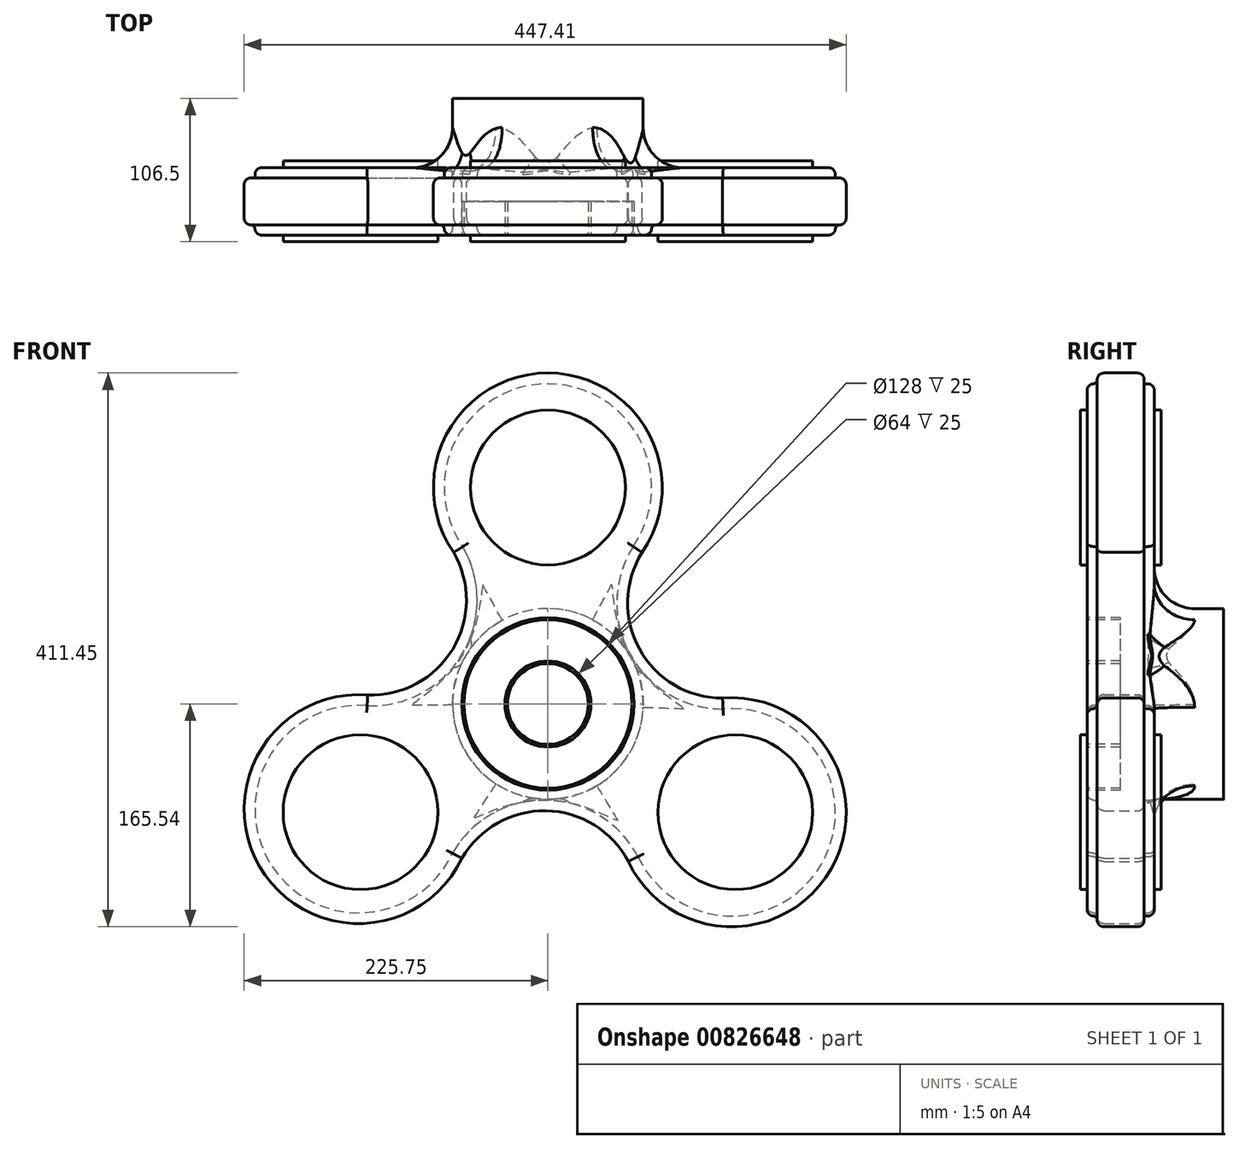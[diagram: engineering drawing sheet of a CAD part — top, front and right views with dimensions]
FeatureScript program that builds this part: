
annotation { "Feature Type Name" : "Feature", "Feature Type Description" : "" }
export const myFeature = defineFeature(function(context is Context, id is Id, definition is map)
    precondition{}
    {
        {
            var Q0;
            Q0=qCreatedBy(makeId("Front.planeOp"),FACE);
            var sketch = newSketch(context, id + "F0", { "sketchPlane" : qUnion([Q0])});
            skLineSegment(sketch, "E0", {"start": v(-407.93, 0) * mm, "end": v(423.02, 0) * mm, "construction": true});
            skLineSegment(sketch, "E1", {"start": v(-410.58, 247) * mm, "end": v(450.17, 247) * mm, "construction": true});
            skLineSegment(sketch, "E2", {"start": v(0, -266.9) * mm, "end": v(0, 261.2) * mm, "construction": true});
            skLineSegment(sketch, "E3", {"start": v(0, 0) * mm, "end": v(-359.58, -207.6) * mm, "construction": true});
            skLineSegment(sketch, "E4", {"start": v(0, 0) * mm, "end": v(372.56, -215.1) * mm, "construction": true});
            skCircle(sketch, "E5", {"center": v(0, 0) * mm, "radius": 50 * mm, "construction": true});
            skCircle(sketch, "E6", {"center": v(0, 160.84) * mm, "radius": 85 * mm, "construction": true});
            skCircle(sketch, "E7.1.0", {"center": v(-139.3, -80.42) * mm, "radius": 85 * mm, "construction": true});
            skCircle(sketch, "E7.2.0", {"center": v(139.3, -80.42) * mm, "radius": 85 * mm, "construction": true});
            skCircle(sketch, "E8", {"center": v(0, -149.9) * mm, "radius": 70 * mm, "construction": true});
            skCircle(sketch, "E9.1.0", {"center": v(129.82, 74.95) * mm, "radius": 70 * mm, "construction": true});
            skCircle(sketch, "E9.2.0", {"center": v(-129.82, 74.95) * mm, "radius": 70 * mm, "construction": true});
            skSolve(sketch);
        }
        {
            var Q0;
            Q0=qCreatedBy(makeId("Front.planeOp"),FACE);
            var sketch = newSketch(context, id + "F1", { "sketchPlane" : qUnion([Q0])});
            skPoint(sketch, "E10.0", {"position": v(-129.82, 74.95) * mm});
            skPoint(sketch, "E11.0", {"position": v(0, 160.84) * mm});
            skArc(sketch, "E12", {"start": v(-70.05, 112.58) * mm, "mid": v(-75.3, 200.4) * mm, "end": v(0, 245.9) * mm});
            skArc(sketch, "E13.MirrorCS", {"start": v(70.05, 112.58) * mm, "mid": v(75.3, 200.4) * mm, "end": v(0, 245.9) * mm});
            skArc(sketch, "E14.MirrorCS", {"start": v(70.05, 112.58) * mm, "mid": v(68, 40.82) * mm, "end": v(129.82, 4.32) * mm});
            skArc(sketch, "E15.1.0", {"start": v(-63.87, -114.64) * mm, "mid": v(-137.3, -163.1) * mm, "end": v(-214.36, -120.64) * mm});
            skArc(sketch, "E15.1.1", {"start": v(-133.92, 6.7) * mm, "mid": v(-212.6, -32.67) * mm, "end": v(-214.36, -120.64) * mm});
            skArc(sketch, "E15.1.2", {"start": v(-133.92, 6.7) * mm, "mid": v(-70.74, 40.79) * mm, "end": v(-70.05, 112.58) * mm});
            skArc(sketch, "E15.2.0", {"start": v(129.82, 4.32) * mm, "mid": v(208.5, -35.04) * mm, "end": v(210.26, -123) * mm});
            skArc(sketch, "E15.2.1", {"start": v(59.77, -117) * mm, "mid": v(133.2, -165.47) * mm, "end": v(210.26, -123) * mm});
            skArc(sketch, "E15.2.2", {"start": v(59.77, -117) * mm, "mid": v(-1.35, -79.34) * mm, "end": v(-63.87, -114.64) * mm});
            skPoint(sketch, "E15.center", {"position": v(-1.37, 0.75) * mm});
            skSolve(sketch);
        }
        {
            var Q0;
            Q0 = qSketchRegion(id + "F1", true);
            extrude(context, id + "F2", {"entities" : qUnion([Q0]), "endBound" : BoundingType.SYMMETRIC, "depth" : 35 * mm, "offsetDistance" : 25 * mm});
        }
        {
            var Q0;
            Q0=qCreatedBy(makeId("Front.planeOp"),FACE);
            var sketch = newSketch(context, id + "F3", { "sketchPlane" : qUnion([Q0])});
            skPoint(sketch, "E16.0", {"position": v(0, 160.84) * mm});
            skCircle(sketch, "E17", {"center": v(0, 160.84) * mm, "radius": 57.5 * mm});
            skCircle(sketch, "E18", {"center": v(0, 160.84) * mm, "radius": 50 * mm});
            skCircle(sketch, "E19.1.0", {"center": v(-139.3, -80.42) * mm, "radius": 57.5 * mm});
            skCircle(sketch, "E19.1.1", {"center": v(-139.3, -80.42) * mm, "radius": 50 * mm});
            skCircle(sketch, "E19.2.0", {"center": v(139.3, -80.42) * mm, "radius": 57.5 * mm});
            skCircle(sketch, "E19.2.1", {"center": v(139.3, -80.42) * mm, "radius": 50 * mm});
            skPoint(sketch, "E19.center", {"position": v(0, 0) * mm});
            skSolve(sketch);
        }
        {
            var Q0;
            Q0 = qSketchRegion(id + "F3", true);
            extrude(context, id + "F4", {"entities" : qUnion([Q0]), "endBound" : BoundingType.SYMMETRIC, "depth" : 60 * mm, "offsetDistance" : 25 * mm});
        }
        {
            var Q0;
            Q0=qCreatedBy(makeId("Front.planeOp"),FACE);
            var sketch = newSketch(context, id + "F5", { "sketchPlane" : qUnion([Q0])});
            skPoint(sketch, "E20.0", {"position": v(0, 160.84) * mm});
            skCircle(sketch, "E21", {"center": v(0, 160.84) * mm, "radius": 32.5 * mm});
            skCircle(sketch, "E22", {"center": v(0, 160.84) * mm, "radius": 17.5 * mm});
            skCircle(sketch, "E23.1.0", {"center": v(-139.3, -80.42) * mm, "radius": 32.5 * mm});
            skCircle(sketch, "E23.1.1", {"center": v(-139.3, -80.42) * mm, "radius": 17.5 * mm});
            skCircle(sketch, "E23.2.0", {"center": v(139.3, -80.42) * mm, "radius": 32.5 * mm});
            skCircle(sketch, "E23.2.1", {"center": v(139.3, -80.42) * mm, "radius": 17.5 * mm});
            skPoint(sketch, "E23.center", {"position": v(0, 0) * mm});
            skSolve(sketch);
        }
        {
            var Q0;
            Q0 = qSketchRegion(id + "F5", true);
            extrude(context, id + "F6", {"entities" : qUnion([Q0]), "endBound" : BoundingType.SYMMETRIC, "depth" : 60 * mm, "offsetDistance" : 25 * mm});
        }
        {
            var Q0;
            Q0=qCreatedBy(makeId("Front.planeOp"),FACE);
            var sketch = newSketch(context, id + "F7", { "sketchPlane" : qUnion([Q0])});
            skCircle(sketch, "E24.0", {"center": v(0, 160.84) * mm, "radius": 50 * mm});
            skCircle(sketch, "E25.0", {"center": v(0, 160.84) * mm, "radius": 32.5 * mm});
            skCircle(sketch, "E26.0", {"center": v(-139.3, -80.42) * mm, "radius": 50 * mm});
            skCircle(sketch, "E27.0", {"center": v(-139.3, -80.42) * mm, "radius": 32.5 * mm});
            skCircle(sketch, "E28.0", {"center": v(139.3, -80.42) * mm, "radius": 32.5 * mm});
            skCircle(sketch, "E29.0", {"center": v(139.3, -80.42) * mm, "radius": 50 * mm});
            skCircle(sketch, "E30.0", {"center": v(0, 160.84) * mm, "radius": 17.5 * mm});
            skCircle(sketch, "E31.0", {"center": v(-139.3, -80.42) * mm, "radius": 17.5 * mm});
            skCircle(sketch, "E32.0", {"center": v(139.3, -80.42) * mm, "radius": 17.5 * mm});
            skSolve(sketch);
        }
        {
            var Q0;
            Q0 = qSketchRegion(id + "F7", true);
            extrude(context, id + "F8", {"entities" : qUnion([Q0]), "operationType" : NewBodyOperationType.ADD, "endBound" : BoundingType.SYMMETRIC, "depth" : 60 * mm, "offsetDistance" : 25 * mm});
        }
        {
            var Q0;
            Q0=qCreatedBy(makeId("Front.planeOp"),FACE);
            var sketch = newSketch(context, id + "F9", { "sketchPlane" : qUnion([Q0])});
            skCircle(sketch, "E33.0", {"center": v(0, 160.84) * mm, "radius": 17.5 * mm});
            skCircle(sketch, "E33.1", {"center": v(-139.3, -80.42) * mm, "radius": 17.5 * mm});
            skCircle(sketch, "E33.2", {"center": v(139.3, -80.42) * mm, "radius": 17.5 * mm});
            skSolve(sketch);
        }
        {
            var Q0;
            Q0 = qSketchRegion(id + "F9", true);
            extrude(context, id + "F10", {"entities" : qUnion([Q0]), "operationType" : NewBodyOperationType.ADD, "endBound" : BoundingType.SYMMETRIC, "depth" : 60 * mm, "offsetDistance" : 25 * mm});
        }
        {
            var Q0;
            {var subQ0=sQuery(id+"F1.wireOp",EDGE,"E15.1.1");var subQ1=sQuery(id+"F1.wireOp",EDGE,"E15.1.0");var subQ2=sQuery(id+"F1.wireOp",EDGE,"E14.MirrorCS");var subQ3=sQuery(id+"F1.wireOp",EDGE,"E15.1.2");var subQ4=sQuery(id+"F1.wireOp",EDGE,"E13.MirrorCS");var subQ5=sQuery(id+"F1.wireOp",EDGE,"E12");var subQ6=sQuery(id+"F1.wireOp",EDGE,"E15.2.1");var subQ7=sQuery(id+"F1.wireOp",EDGE,"E15.2.0");var subQ8=sQuery(id+"F1.wireOp",EDGE,"E15.2.2");Q0=makeQuery(id+"F8.boolean.opBoolean","SPLIT",FACE,{"disambiguationData":[TD([makeQuery(id+"F2.opExtrude","SWEPT_FACE",FACE,{"disambiguationData":[OSD([subQ2])]})])],"derivedFrom":makeQuery(id+"F2.opExtrude","CAP_FACE",FACE,{"disambiguationData":[OSD([subQ5,subQ4,subQ2,subQ1,subQ0,subQ3,subQ7,subQ6,subQ8])],"isStart":true})});}
            var sketch = newSketch(context, id + "F11", { "sketchPlane" : qUnion([Q0])});
            skCircle(sketch, "E34", {"center": v(0, 0) * mm, "radius": 70.83 * mm});
            skSolve(sketch);
        }
        {
            var Q0;
            Q0 = qSketchRegion(id + "F11", true);
            extrude(context, id + "F12", {"entities" : qUnion([Q0]), "operationType" : NewBodyOperationType.ADD, "depth" : 59 * mm, "offsetDistance" : 25 * mm});
        }
        {
            var Q0;
            Q0=qCreatedBy(makeId("Front.planeOp"),FACE);
            var sketch = newSketch(context, id + "F13", { "sketchPlane" : qUnion([Q0])});
            skArc(sketch, "E35.0", {"start": v(63.37, 116.99) * mm, "mid": v(61.03, 36.88) * mm, "end": v(130.16, -3.67) * mm});
            skArc(sketch, "E35.1", {"start": v(-134.4, -1.3) * mm, "mid": v(-63.85, 36.73) * mm, "end": v(-63.3, 116.87) * mm});
            skArc(sketch, "E35.2", {"start": v(-134.4, -1.3) * mm, "mid": v(-207.4, -116.7) * mm, "end": v(-70.96, -110.93) * mm});
            skArc(sketch, "E35.3", {"start": v(63.37, 116.99) * mm, "mid": v(-0.07, 237.9) * mm, "end": v(-63.3, 116.87) * mm});
            skArc(sketch, "E35.4", {"start": v(66.93, -113.43) * mm, "mid": v(-1.28, -71.34) * mm, "end": v(-70.96, -110.93) * mm});
            skArc(sketch, "E35.5", {"start": v(66.93, -113.43) * mm, "mid": v(203.37, -118.94) * mm, "end": v(130.16, -3.67) * mm});
            skCircle(sketch, "E36.0", {"center": v(0, 160.84) * mm, "radius": 57.5 * mm});
            skCircle(sketch, "E37.0", {"center": v(-139.3, -80.42) * mm, "radius": 57.5 * mm});
            skCircle(sketch, "E38.0", {"center": v(139.3, -80.42) * mm, "radius": 57.5 * mm});
            skSolve(sketch);
        }
        {
            var Q0;
            Q0 = qSketchRegion(id + "F13", true);
            extrude(context, id + "F14", {"entities" : qUnion([Q0]), "operationType" : NewBodyOperationType.ADD, "endBound" : BoundingType.SYMMETRIC, "depth" : 50 * mm, "offsetDistance" : 25 * mm});
        }
        {
            var Q0;
            Q0=makeQuery(id+"F14.opExtrude","CAP_FACE",FACE,{"disambiguationData":[OSD([sQuery(id+"F13.wireOp",EDGE,"E35.0"),sQuery(id+"F13.wireOp",EDGE,"E35.1"),sQuery(id+"F13.wireOp",EDGE,"E35.2"),sQuery(id+"F13.wireOp",EDGE,"E35.3"),sQuery(id+"F13.wireOp",EDGE,"E35.4"),sQuery(id+"F13.wireOp",EDGE,"E35.5"),sQuery(id+"F13.wireOp",EDGE,"E36.0"),sQuery(id+"F13.wireOp",EDGE,"E37.0"),sQuery(id+"F13.wireOp",EDGE,"E38.0")])],"isStart":false});
            var sketch = newSketch(context, id + "F15", { "sketchPlane" : qUnion([Q0])});
            skCircle(sketch, "E39", {"center": v(0, 0) * mm, "radius": 64 * mm});
            skSolve(sketch);
        }
        {
            var Q0;
            Q0 = qSketchRegion(id + "F15", true);
            extrude(context, id + "F16", {"entities" : qUnion([Q0]), "operationType" : NewBodyOperationType.REMOVE, "oppositeDirection" : true, "depth" : 25 * mm, "offsetDistance" : 25 * mm});
        }
        {
            var Q0;
            Q0=makeQuery(id+"F14.opExtrude","CAP_FACE",FACE,{"disambiguationData":[OSD([sQuery(id+"F13.wireOp",EDGE,"E35.0"),sQuery(id+"F13.wireOp",EDGE,"E35.1"),sQuery(id+"F13.wireOp",EDGE,"E35.2"),sQuery(id+"F13.wireOp",EDGE,"E35.3"),sQuery(id+"F13.wireOp",EDGE,"E35.4"),sQuery(id+"F13.wireOp",EDGE,"E35.5"),sQuery(id+"F13.wireOp",EDGE,"E36.0"),sQuery(id+"F13.wireOp",EDGE,"E37.0"),sQuery(id+"F13.wireOp",EDGE,"E38.0")])],"isStart":false});
            var sketch = newSketch(context, id + "F17", { "sketchPlane" : qUnion([Q0])});
            skCircle(sketch, "E40", {"center": v(0, 0) * mm, "radius": 62.5 * mm});
            skSolve(sketch);
        }
        {
            var Q0;
            Q0 = qSketchRegion(id + "F17", true);
            extrude(context, id + "F18", {"entities" : qUnion([Q0]), "operationType" : NewBodyOperationType.ADD, "oppositeDirection" : true, "depth" : 37 * mm, "offsetDistance" : 25 * mm});
        }
        {
            var Q0;
            Q0=makeQuery(id+"F2.opExtrude","CAP_EDGE",EDGE,{"disambiguationData":[OSD([sQuery(id+"F1.wireOp",EDGE,"E12"),sQuery(id+"F1.wireOp",EDGE,"E13.MirrorCS")])],"isStart":false});
            var Q1;
            Q1=makeQuery(id+"F2.opExtrude","CAP_EDGE",EDGE,{"disambiguationData":[OSD([sQuery(id+"F1.wireOp",EDGE,"E15.1.0"),sQuery(id+"F1.wireOp",EDGE,"E15.1.1")])],"isStart":false});
            var Q2;
            Q2=makeQuery(id+"F2.opExtrude","CAP_EDGE",EDGE,{"disambiguationData":[OSD([sQuery(id+"F1.wireOp",EDGE,"E15.2.0"),sQuery(id+"F1.wireOp",EDGE,"E15.2.1")])],"isStart":false});
            var Q3;
            Q3=makeQuery(id+"F2.opExtrude","CAP_EDGE",EDGE,{"disambiguationData":[OSD([sQuery(id+"F1.wireOp",EDGE,"E15.2.0"),sQuery(id+"F1.wireOp",EDGE,"E15.2.1")])],"isStart":true});
            var Q4;
            Q4=makeQuery(id+"F2.opExtrude","CAP_EDGE",EDGE,{"disambiguationData":[OSD([sQuery(id+"F1.wireOp",EDGE,"E15.1.0"),sQuery(id+"F1.wireOp",EDGE,"E15.1.1")])],"isStart":true});
            var Q5;
            Q5=makeQuery(id+"FlsZefj5eaNXOrE_7.opFillet","BLEND_EDGE",EDGE,{"blendedFrom":[makeQuery(id+"F12.opExtrude","CAP_EDGE",EDGE,{"disambiguationData":[OSD([sQuery(id+"F11.wireOp",EDGE,"E34")])],"isStart":true}),makeQuery(id+"F2.opExtrude","SWEPT_FACE",FACE,{"disambiguationData":[OSD([sQuery(id+"F1.wireOp",EDGE,"E15.2.2")])]})],"blendedInto":[makeQuery(id+"F2.opExtrude","SWEPT_FACE",FACE,{"disambiguationData":[OSD([sQuery(id+"F1.wireOp",EDGE,"E15.2.2")])]})]});
            var Q6;
            Q6=makeQuery(id+"FlsZefj5eaNXOrE_7.opFillet","BLEND_EDGE",EDGE,{"blendedFrom":[makeQuery(id+"F12.opExtrude","CAP_EDGE",EDGE,{"disambiguationData":[OSD([sQuery(id+"F11.wireOp",EDGE,"E34")])],"isStart":true}),makeQuery(id+"F2.opExtrude","SWEPT_FACE",FACE,{"disambiguationData":[OSD([sQuery(id+"F1.wireOp",EDGE,"E14.MirrorCS")])]})],"blendedInto":[makeQuery(id+"F2.opExtrude","SWEPT_FACE",FACE,{"disambiguationData":[OSD([sQuery(id+"F1.wireOp",EDGE,"E14.MirrorCS")])]})]});
            var Q7;
            Q7=makeQuery(id+"F2.opExtrude","CAP_EDGE",EDGE,{"disambiguationData":[OSD([sQuery(id+"F1.wireOp",EDGE,"E12"),sQuery(id+"F1.wireOp",EDGE,"E13.MirrorCS")])],"isStart":true});
            var Q8;
            Q8=makeQuery(id+"FlsZefj5eaNXOrE_7.opFillet","BLEND_EDGE",EDGE,{"blendedFrom":[makeQuery(id+"F12.opExtrude","CAP_EDGE",EDGE,{"disambiguationData":[OSD([sQuery(id+"F11.wireOp",EDGE,"E34")])],"isStart":true}),makeQuery(id+"F2.opExtrude","SWEPT_FACE",FACE,{"disambiguationData":[OSD([sQuery(id+"F1.wireOp",EDGE,"E15.1.2")])]})],"blendedInto":[makeQuery(id+"F2.opExtrude","SWEPT_FACE",FACE,{"disambiguationData":[OSD([sQuery(id+"F1.wireOp",EDGE,"E15.1.2")])]})]});
            fillet(context, id + "F19", {"entities" : qUnion([Q0, Q1, Q2, Q3, Q4, Q5, Q6, Q7, Q8]), "radius" : 5 * mm, "tangentPropagation" : true, "allowEdgeOverflow" : false});
        }
        {
            var Q0;
            {var subQ0=sQuery(id+"F1.wireOp",EDGE,"E15.1.1");var subQ1=sQuery(id+"F1.wireOp",EDGE,"E15.1.0");var subQ2=sQuery(id+"F1.wireOp",EDGE,"E14.MirrorCS");var subQ3=sQuery(id+"F1.wireOp",EDGE,"E15.1.2");var subQ4=sQuery(id+"F1.wireOp",EDGE,"E13.MirrorCS");var subQ5=sQuery(id+"F1.wireOp",EDGE,"E12");var subQ6=sQuery(id+"F1.wireOp",EDGE,"E15.2.1");var subQ7=sQuery(id+"F1.wireOp",EDGE,"E15.2.0");var subQ8=sQuery(id+"F1.wireOp",EDGE,"E15.2.2");Q0=makeQuery(id+"F14.boolean.opBoolean","INTERSECT",EDGE,{"derivedFrom":[makeQuery(id+"F8.boolean.opBoolean","SPLIT",FACE,{"disambiguationData":[TD([makeQuery(id+"F2.opExtrude","SWEPT_FACE",FACE,{"disambiguationData":[OSD([subQ2])]})])],"derivedFrom":makeQuery(id+"F2.opExtrude","CAP_FACE",FACE,{"disambiguationData":[OSD([subQ5,subQ4,subQ2,subQ1,subQ0,subQ3,subQ7,subQ6,subQ8])],"isStart":false})}),makeQuery(id+"F14.opExtrude","SWEPT_FACE",FACE,{"disambiguationData":[OSD([sQuery(id+"F13.wireOp",EDGE,"E35.3")])]})]});}
            var Q1;
            {var subQ0=sQuery(id+"F1.wireOp",EDGE,"E15.1.1");var subQ1=sQuery(id+"F1.wireOp",EDGE,"E15.1.0");var subQ2=sQuery(id+"F1.wireOp",EDGE,"E14.MirrorCS");var subQ3=sQuery(id+"F1.wireOp",EDGE,"E15.1.2");var subQ4=sQuery(id+"F1.wireOp",EDGE,"E13.MirrorCS");var subQ5=sQuery(id+"F1.wireOp",EDGE,"E12");var subQ6=sQuery(id+"F1.wireOp",EDGE,"E15.2.1");var subQ7=sQuery(id+"F1.wireOp",EDGE,"E15.2.0");var subQ8=sQuery(id+"F1.wireOp",EDGE,"E15.2.2");Q1=makeQuery(id+"F14.boolean.opBoolean","INTERSECT",EDGE,{"derivedFrom":[makeQuery(id+"F8.boolean.opBoolean","SPLIT",FACE,{"disambiguationData":[TD([makeQuery(id+"F2.opExtrude","SWEPT_FACE",FACE,{"disambiguationData":[OSD([subQ2])]})])],"derivedFrom":makeQuery(id+"F2.opExtrude","CAP_FACE",FACE,{"disambiguationData":[OSD([subQ5,subQ4,subQ2,subQ1,subQ0,subQ3,subQ7,subQ6,subQ8])],"isStart":false})}),makeQuery(id+"F14.opExtrude","SWEPT_FACE",FACE,{"disambiguationData":[OSD([sQuery(id+"F13.wireOp",EDGE,"E35.1")])]})]});}
            var Q2;
            {var subQ0=sQuery(id+"F1.wireOp",EDGE,"E15.1.1");var subQ1=sQuery(id+"F1.wireOp",EDGE,"E15.1.0");var subQ2=sQuery(id+"F1.wireOp",EDGE,"E14.MirrorCS");var subQ3=sQuery(id+"F1.wireOp",EDGE,"E15.1.2");var subQ4=sQuery(id+"F1.wireOp",EDGE,"E13.MirrorCS");var subQ5=sQuery(id+"F1.wireOp",EDGE,"E12");var subQ6=sQuery(id+"F1.wireOp",EDGE,"E15.2.1");var subQ7=sQuery(id+"F1.wireOp",EDGE,"E15.2.0");var subQ8=sQuery(id+"F1.wireOp",EDGE,"E15.2.2");Q2=makeQuery(id+"F14.boolean.opBoolean","INTERSECT",EDGE,{"derivedFrom":[makeQuery(id+"F8.boolean.opBoolean","SPLIT",FACE,{"disambiguationData":[TD([makeQuery(id+"F2.opExtrude","SWEPT_FACE",FACE,{"disambiguationData":[OSD([subQ2])]})])],"derivedFrom":makeQuery(id+"F2.opExtrude","CAP_FACE",FACE,{"disambiguationData":[OSD([subQ5,subQ4,subQ2,subQ1,subQ0,subQ3,subQ7,subQ6,subQ8])],"isStart":false})}),makeQuery(id+"F14.opExtrude","SWEPT_FACE",FACE,{"disambiguationData":[OSD([sQuery(id+"F13.wireOp",EDGE,"E35.2")])]})]});}
            var Q3;
            {var subQ0=sQuery(id+"F1.wireOp",EDGE,"E15.1.1");var subQ1=sQuery(id+"F1.wireOp",EDGE,"E15.1.0");var subQ2=sQuery(id+"F1.wireOp",EDGE,"E14.MirrorCS");var subQ3=sQuery(id+"F1.wireOp",EDGE,"E15.1.2");var subQ4=sQuery(id+"F1.wireOp",EDGE,"E13.MirrorCS");var subQ5=sQuery(id+"F1.wireOp",EDGE,"E12");var subQ6=sQuery(id+"F1.wireOp",EDGE,"E15.2.1");var subQ7=sQuery(id+"F1.wireOp",EDGE,"E15.2.0");var subQ8=sQuery(id+"F1.wireOp",EDGE,"E15.2.2");Q3=makeQuery(id+"F14.boolean.opBoolean","INTERSECT",EDGE,{"derivedFrom":[makeQuery(id+"F8.boolean.opBoolean","SPLIT",FACE,{"disambiguationData":[TD([makeQuery(id+"F2.opExtrude","SWEPT_FACE",FACE,{"disambiguationData":[OSD([subQ2])]})])],"derivedFrom":makeQuery(id+"F2.opExtrude","CAP_FACE",FACE,{"disambiguationData":[OSD([subQ5,subQ4,subQ2,subQ1,subQ0,subQ3,subQ7,subQ6,subQ8])],"isStart":false})}),makeQuery(id+"F14.opExtrude","SWEPT_FACE",FACE,{"disambiguationData":[OSD([sQuery(id+"F13.wireOp",EDGE,"E35.4")])]})]});}
            var Q4;
            {var subQ0=sQuery(id+"F1.wireOp",EDGE,"E15.1.1");var subQ1=sQuery(id+"F1.wireOp",EDGE,"E15.1.0");var subQ2=sQuery(id+"F1.wireOp",EDGE,"E14.MirrorCS");var subQ3=sQuery(id+"F1.wireOp",EDGE,"E15.1.2");var subQ4=sQuery(id+"F1.wireOp",EDGE,"E13.MirrorCS");var subQ5=sQuery(id+"F1.wireOp",EDGE,"E12");var subQ6=sQuery(id+"F1.wireOp",EDGE,"E15.2.1");var subQ7=sQuery(id+"F1.wireOp",EDGE,"E15.2.0");var subQ8=sQuery(id+"F1.wireOp",EDGE,"E15.2.2");Q4=makeQuery(id+"F14.boolean.opBoolean","INTERSECT",EDGE,{"derivedFrom":[makeQuery(id+"F8.boolean.opBoolean","SPLIT",FACE,{"disambiguationData":[TD([makeQuery(id+"F2.opExtrude","SWEPT_FACE",FACE,{"disambiguationData":[OSD([subQ2])]})])],"derivedFrom":makeQuery(id+"F2.opExtrude","CAP_FACE",FACE,{"disambiguationData":[OSD([subQ5,subQ4,subQ2,subQ1,subQ0,subQ3,subQ7,subQ6,subQ8])],"isStart":false})}),makeQuery(id+"F14.opExtrude","SWEPT_FACE",FACE,{"disambiguationData":[OSD([sQuery(id+"F13.wireOp",EDGE,"E35.5")])]})]});}
            var Q5;
            {var subQ0=sQuery(id+"F1.wireOp",EDGE,"E15.1.1");var subQ1=sQuery(id+"F1.wireOp",EDGE,"E15.1.0");var subQ2=sQuery(id+"F1.wireOp",EDGE,"E14.MirrorCS");var subQ3=sQuery(id+"F1.wireOp",EDGE,"E15.1.2");var subQ4=sQuery(id+"F1.wireOp",EDGE,"E13.MirrorCS");var subQ5=sQuery(id+"F1.wireOp",EDGE,"E12");var subQ6=sQuery(id+"F1.wireOp",EDGE,"E15.2.1");var subQ7=sQuery(id+"F1.wireOp",EDGE,"E15.2.0");var subQ8=sQuery(id+"F1.wireOp",EDGE,"E15.2.2");Q5=makeQuery(id+"F14.boolean.opBoolean","INTERSECT",EDGE,{"derivedFrom":[makeQuery(id+"F8.boolean.opBoolean","SPLIT",FACE,{"disambiguationData":[TD([makeQuery(id+"F2.opExtrude","SWEPT_FACE",FACE,{"disambiguationData":[OSD([subQ2])]})])],"derivedFrom":makeQuery(id+"F2.opExtrude","CAP_FACE",FACE,{"disambiguationData":[OSD([subQ5,subQ4,subQ2,subQ1,subQ0,subQ3,subQ7,subQ6,subQ8])],"isStart":false})}),makeQuery(id+"F14.opExtrude","SWEPT_FACE",FACE,{"disambiguationData":[OSD([sQuery(id+"F13.wireOp",EDGE,"E35.0")])]})]});}
            fillet(context, id + "F20", {"entities" : qUnion([Q0, Q1, Q2, Q3, Q4, Q5]), "radius" : 3 * mm, "tangentPropagation" : true, "allowEdgeOverflow" : false});
        }
        {
            var Q0;
            Q0=makeQuery(id+"F14.opExtrude","CAP_EDGE",EDGE,{"disambiguationData":[OSD([sQuery(id+"F13.wireOp",EDGE,"E35.1")])],"isStart":false});
            var Q1;
            Q1=makeQuery(id+"F14.opExtrude","CAP_EDGE",EDGE,{"disambiguationData":[OSD([sQuery(id+"F13.wireOp",EDGE,"E35.3")])],"isStart":false});
            var Q2;
            Q2=makeQuery(id+"F14.opExtrude","CAP_EDGE",EDGE,{"disambiguationData":[OSD([sQuery(id+"F13.wireOp",EDGE,"E35.5")])],"isStart":false});
            var Q3;
            Q3=makeQuery(id+"F14.opExtrude","CAP_EDGE",EDGE,{"disambiguationData":[OSD([sQuery(id+"F13.wireOp",EDGE,"E35.2")])],"isStart":false});
            fillet(context, id + "F21", {"entities" : qUnion([Q0, Q1, Q2, Q3]), "radius" : 5 * mm, "tangentPropagation" : true, "allowEdgeOverflow" : false});
        }
        {
            var Q0;
            Q0=makeQuery(id+"F18.opExtrude","CAP_FACE",FACE,{"disambiguationData":[OSD([sQuery(id+"F17.wireOp",EDGE,"E40")])],"isStart":true});
            var sketch = newSketch(context, id + "F22", { "sketchPlane" : qUnion([Q0])});
            skCircle(sketch, "E41", {"center": v(0, 0) * mm, "radius": 30 * mm});
            skCircle(sketch, "E42.0", {"center": v(0, 0) * mm, "radius": 32 * mm});
            skSolve(sketch);
        }
        {
            var Q0;
            Q0 = qSketchRegion(id + "F22", true);
            var Q1;
            Q1 = qConstructionFilter(qBodyType(qCreatedBy(id + "F22" ,EDGE), BodyType.WIRE), ConstructionObject.NO);
            extrude(context, id + "F23", {"entities" : qUnion([Q0]), "operationType" : NewBodyOperationType.REMOVE, "surfaceEntities" : qUnion([Q1]), "oppositeDirection" : true, "depth" : 25 * mm, "offsetDistance" : 25 * mm});
        }
        {
            var Q0;
            Q0=makeQuery(id+"F16.boolean.opBoolean","COPY",EDGE,{"derivedFrom":makeQuery(id+"F16.opExtrude","CAP_EDGE",EDGE,{"disambiguationData":[OSD([sQuery(id+"F15.wireOp",EDGE,"E39")])],"isStart":true})});
            var Q1;
            Q1=makeQuery(id+"F18.opExtrude","CAP_EDGE",EDGE,{"disambiguationData":[OSD([sQuery(id+"F17.wireOp",EDGE,"E40")])],"isStart":true});
            var Q2;
            Q2=makeQuery(id+"F23.boolean.opBoolean","COPY",EDGE,{"derivedFrom":makeQuery(id+"F23.opExtrude","CAP_EDGE",EDGE,{"disambiguationData":[OSD([sQuery(id+"F22.wireOp",EDGE,"E42.0")])],"isStart":true})});
            var Q3;
            Q3=makeQuery(id+"F23.boolean.opBoolean","COPY",EDGE,{"derivedFrom":makeQuery(id+"F23.opExtrude","CAP_EDGE",EDGE,{"disambiguationData":[OSD([sQuery(id+"F22.wireOp",EDGE,"E41")])],"isStart":true})});
            fillet(context, id + "F24", {"entities" : qUnion([Q0, Q1, Q2, Q3]), "radius" : 2 * mm, "tangentPropagation" : true, "allowEdgeOverflow" : false});
        }
        {
            var Q0;
            Q0=makeQuery(id+"F14.opExtrude","CAP_EDGE",EDGE,{"disambiguationData":[OSD([sQuery(id+"F13.wireOp",EDGE,"E35.3")])],"isStart":true});
            var Q1;
            Q1=makeQuery(id+"F14.opExtrude","CAP_EDGE",EDGE,{"disambiguationData":[OSD([sQuery(id+"F13.wireOp",EDGE,"E35.2")])],"isStart":true});
            var Q2;
            Q2=makeQuery(id+"F14.opExtrude","CAP_EDGE",EDGE,{"disambiguationData":[OSD([sQuery(id+"F13.wireOp",EDGE,"E35.5")])],"isStart":true});
            fillet(context, id + "F25", {"entities" : qUnion([Q0, Q1, Q2]), "radius" : 5 * mm, "tangentPropagation" : true, "allowEdgeOverflow" : false});
        }
        {
            var Q0;
            Q0=makeQuery(id+"F14.boolean.opBoolean","INTERSECT",EDGE,{"derivedFrom":[makeQuery(id+"F12.opExtrude","SWEPT_FACE",FACE,{"disambiguationData":[OSD([sQuery(id+"F11.wireOp",EDGE,"E34")])]}),makeQuery(id+"F14.opExtrude","CAP_FACE",FACE,{"disambiguationData":[OSD([sQuery(id+"F13.wireOp",EDGE,"E35.0"),sQuery(id+"F13.wireOp",EDGE,"E35.1"),sQuery(id+"F13.wireOp",EDGE,"E35.2"),sQuery(id+"F13.wireOp",EDGE,"E35.3"),sQuery(id+"F13.wireOp",EDGE,"E35.4"),sQuery(id+"F13.wireOp",EDGE,"E35.5"),sQuery(id+"F13.wireOp",EDGE,"E36.0"),sQuery(id+"F13.wireOp",EDGE,"E37.0"),sQuery(id+"F13.wireOp",EDGE,"E38.0")])],"isStart":true})]});
            fillet(context, id + "F26", {"entities" : qUnion([Q0]), "radius" : 30 * mm, "tangentPropagation" : true, "allowEdgeOverflow" : false});
        }
    });
